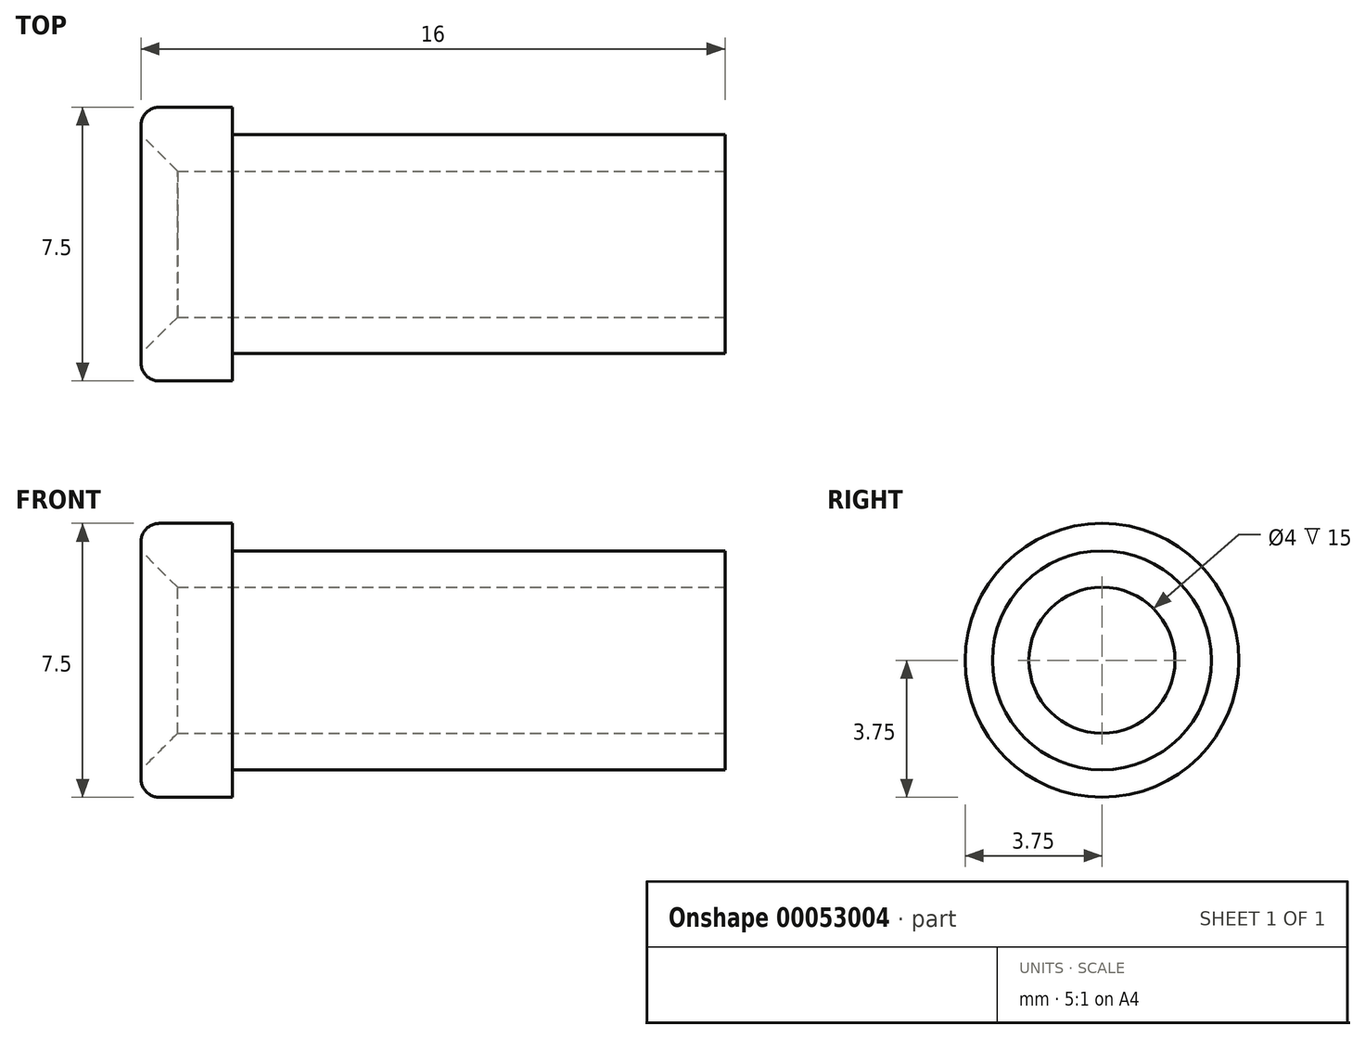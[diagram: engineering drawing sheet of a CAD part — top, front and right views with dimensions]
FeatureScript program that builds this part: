
annotation { "Feature Type Name" : "Feature", "Feature Type Description" : "" }
export const myFeature = defineFeature(function(context is Context, id is Id, definition is map)
    precondition{}
    {
        {
            var Q0;
            Q0=qCreatedBy(makeId("Front.planeOp"),FACE);
            var sketch = newSketch(context, id + "F0", { "sketchPlane" : qUnion([Q0])});
            skLineSegment(sketch, "E0", {"start": v(0, 0) * mm, "end": v(0, 3.75) * mm});
            skLineSegment(sketch, "E1", {"start": v(0, 3.75) * mm, "end": v(2.5, 3.75) * mm});
            skLineSegment(sketch, "E2", {"start": v(2.5, 3.75) * mm, "end": v(2.5, 3) * mm});
            skLineSegment(sketch, "E3", {"start": v(2.5, 3) * mm, "end": v(16, 3) * mm});
            skLineSegment(sketch, "E4", {"start": v(16, 3) * mm, "end": v(16, 0) * mm});
            skLineSegment(sketch, "E5", {"start": v(16, 0) * mm, "end": v(0, 0) * mm});
            skSolve(sketch);
        }
        {
            var Q0;
            Q0=makeQuery(id+"F0.imprint","IMPRINT",FACE,{"disambiguationData":[TD([[makeQuery(id+"F0.imprint","IMPRINT",EDGE,{"derivedFrom":sQuery(id+"F0.wireOp",EDGE,"E0")}),-1.0]])]});
            var Q1;
            Q1=sQuery(id+"F0.wireOp",EDGE,"E5");
            revolve(context, id + "F1", {"entities" : qUnion([Q0]), "axis" : qUnion([Q1]), "revolveType" : RevolveType.FULL});
        }
        {
            var Q0;
            Q0=makeQuery(id+"F1.opRevolve","SWEPT_EDGE",EDGE,{"disambiguationData":[OSD([sQuery(id+"F0.wireOp",EDGE,"E0"),sQuery(id+"F0.wireOp",EDGE,"E1")])]});
            fillet(context, id + "F2", {"entities" : qUnion([Q0]), "radius" : 0.5 * mm, "tangentPropagation" : true, "allowEdgeOverflow" : false});
        }
        {
            var Q0;
            Q0=makeQuery(id+"F1.opRevolve","SWEPT_FACE",FACE,{"disambiguationData":[OSD([sQuery(id+"F0.wireOp",EDGE,"E0")])]});
            var sketch = newSketch(context, id + "F3", { "sketchPlane" : qUnion([Q0])});
            skPoint(sketch, "E6", {"position": v(0, 0) * mm});
            skSolve(sketch);
        }
        {
            var Q0;
            Q0=sQuery(id+"F3.wireOp",VERTEX,"E6");
            var Q1;
            Q1=makeQuery(id+"F1.opRevolve","SWEPT_BODY",BODY,{"disambiguationData":[OSD([sQuery(id+"F0.wireOp",EDGE,"E0"),sQuery(id+"F0.wireOp",EDGE,"E1"),sQuery(id+"F0.wireOp",EDGE,"E2"),sQuery(id+"F0.wireOp",EDGE,"E3"),sQuery(id+"F0.wireOp",EDGE,"E4"),sQuery(id+"F0.wireOp",EDGE,"E5")])]});
            hole(context, id + "F4", {"style" : HoleStyle.C_SINK, "holeDiameter" : 4 * mm, "cSinkDiameter" : 6 * mm, "endStyle" : HoleEndStyle.THROUGH, "locations" : qUnion([Q0]), "scope" : qUnion([Q1]), "cSinkAngle" : 90 * degree});
        }
    });
